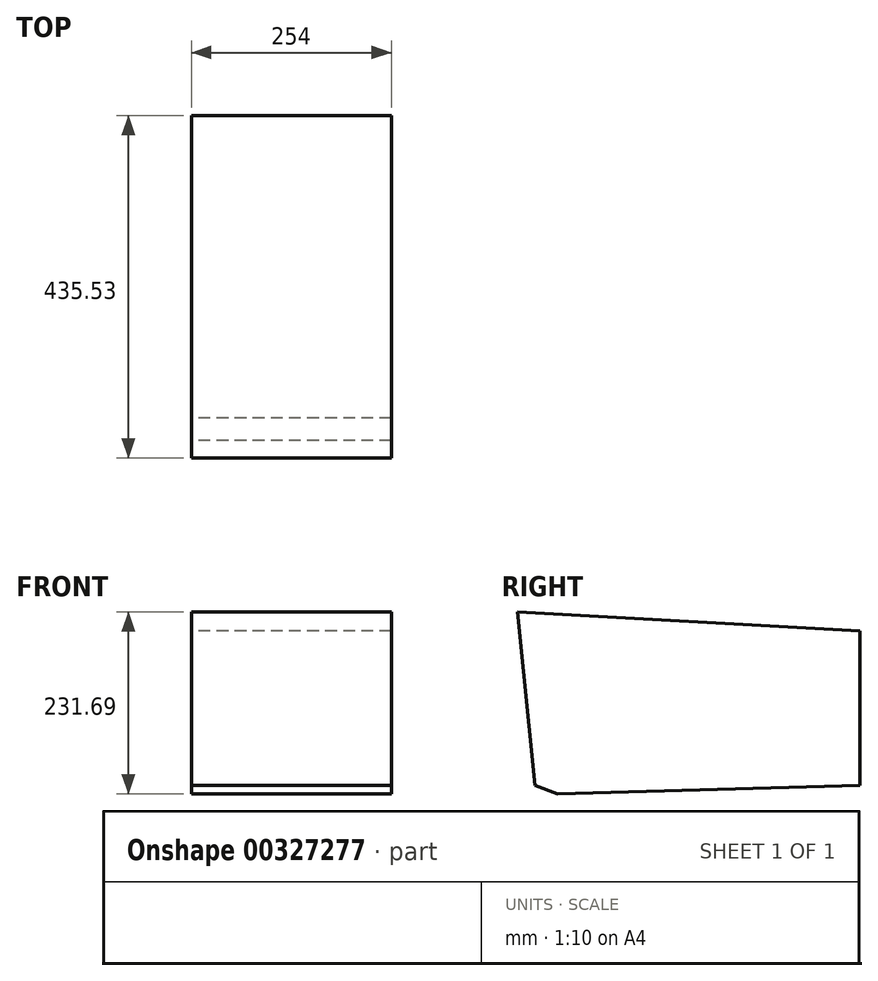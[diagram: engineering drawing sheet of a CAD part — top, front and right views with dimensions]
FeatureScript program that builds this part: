
annotation { "Feature Type Name" : "Feature", "Feature Type Description" : "" }
export const myFeature = defineFeature(function(context is Context, id is Id, definition is map)
    precondition{}
    {
        {
            var Q0;
            Q0=qCreatedBy(makeId("Right.planeOp"),FACE);
            var sketch = newSketch(context, id + "F0", { "sketchPlane" : qUnion([Q0])});
            skLineSegment(sketch, "E0", {"start": v(52.45, 196.21) * mm, "end": v(-383.08, 220.39) * mm});
            skLineSegment(sketch, "E1", {"start": v(-383.08, 220.39) * mm, "end": v(-360.51, 0) * mm});
            skLineSegment(sketch, "E2", {"start": v(-360.51, 0) * mm, "end": v(-332.08, -11.3) * mm});
            skLineSegment(sketch, "E3", {"start": v(-332.08, -11.3) * mm, "end": v(52.45, 0) * mm});
            skLineSegment(sketch, "E4", {"start": v(52.45, 0) * mm, "end": v(52.45, 196.21) * mm});
            skSolve(sketch);
        }
        {
            var Q0;
            Q0=makeQuery(id+"F0.imprint","IMPRINT",FACE,{"disambiguationData":[TD([[makeQuery(id+"F0.imprint","IMPRINT",EDGE,{"derivedFrom":sQuery(id+"F0.wireOp",EDGE,"E0")}),1.0]])]});
            extrude(context, id + "F1", {"entities" : qUnion([Q0]), "depth" : 254 * mm});
        }
    });
